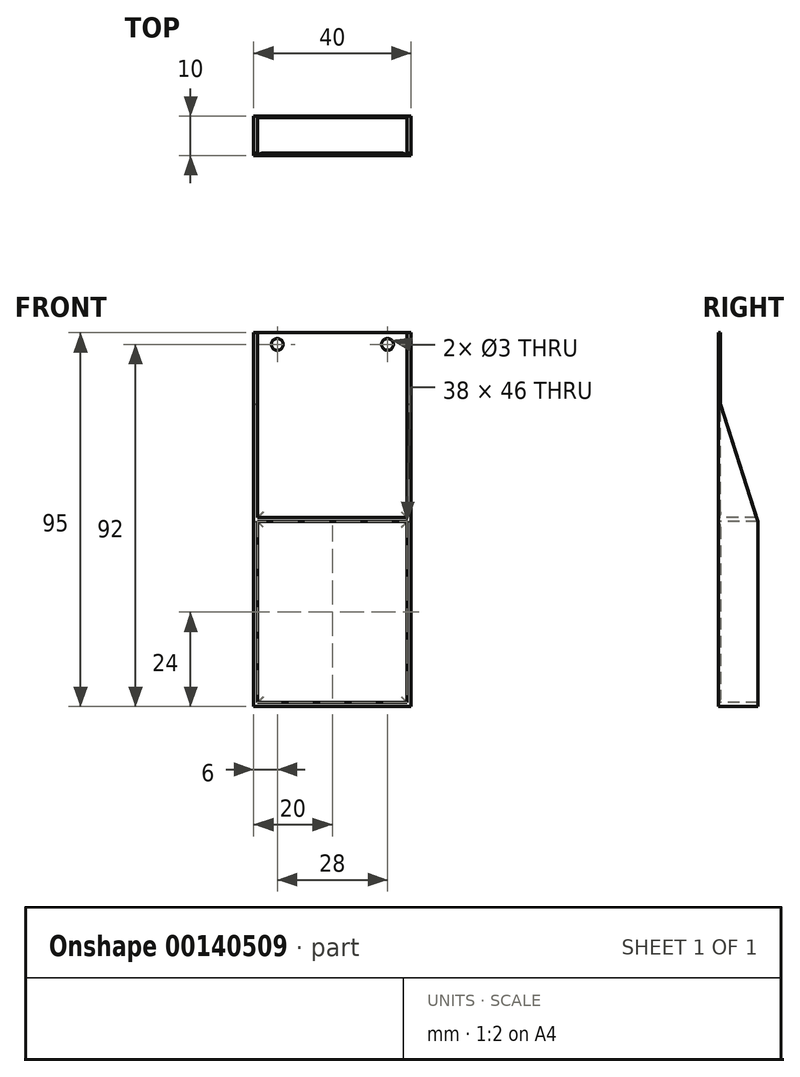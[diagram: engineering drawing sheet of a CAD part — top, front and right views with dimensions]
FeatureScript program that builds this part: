
annotation { "Feature Type Name" : "Feature", "Feature Type Description" : "" }
export const myFeature = defineFeature(function(context is Context, id is Id, definition is map)
    precondition{}
    {
        {
            var Q0;
            Q0=qCreatedBy(makeId("Front.planeOp"),FACE);
            var sketch = newSketch(context, id + "F0", { "sketchPlane" : qUnion([Q0])});
            skLineSegment(sketch, "E0.bottom", {"start": v(20, -47.5) * mm, "end": v(-20, -47.5) * mm});
            skLineSegment(sketch, "E0.top", {"start": v(20, 47.5) * mm, "end": v(-20, 47.5) * mm});
            skLineSegment(sketch, "E0.left", {"start": v(20, -47.5) * mm, "end": v(20, 47.5) * mm});
            skLineSegment(sketch, "E0.right", {"start": v(-20, -47.5) * mm, "end": v(-20, 47.5) * mm});
            skPoint(sketch, "E0.middle", {"position": v(0, 0) * mm});
            skLineSegment(sketch, "E1", {"start": v(-20, 47.5) * mm, "end": v(-19, 47.5) * mm});
            skLineSegment(sketch, "E2", {"start": v(-19, 47.5) * mm, "end": v(-19, 0.5) * mm});
            skLineSegment(sketch, "E3", {"start": v(20, -47.5) * mm, "end": v(19, -47.5) * mm});
            skLineSegment(sketch, "E4", {"start": v(19, -46.5) * mm, "end": v(19, -0.5) * mm});
            skLineSegment(sketch, "E5", {"start": v(-19, -46.5) * mm, "end": v(19, -46.5) * mm});
            skLineSegment(sketch, "E6", {"start": v(-19, 0.5) * mm, "end": v(19, 0.5) * mm});
            skLineSegment(sketch, "E7", {"start": v(19, -0.5) * mm, "end": v(-19, -0.5) * mm});
            skPoint(sketch, "E8.start.orphan", {"position": v(-19, 0) * mm});
            skLineSegment(sketch, "E9.trimOffspring", {"start": v(-19, -0.5) * mm, "end": v(-19, -46.5) * mm});
            skLineSegment(sketch, "E10.trimOffspring", {"start": v(19, 0.5) * mm, "end": v(19, 47.5) * mm});
            skPoint(sketch, "E11.start.orphan", {"position": v(-19, -47.5) * mm});
            skLineSegment(sketch, "E12", {"start": v(19, 47.5) * mm, "end": v(19, 44.5) * mm});
            skCircle(sketch, "E13", {"center": v(-14, 44.5) * mm, "radius": 1.5 * mm});
            skCircle(sketch, "E14", {"center": v(14, 44.5) * mm, "radius": 1.5 * mm});
            skSolve(sketch);
        }
        {
            var Q0;
            Q0=qCreatedBy(makeId("Right.planeOp"),FACE);
            var sketch = newSketch(context, id + "F1", { "sketchPlane" : qUnion([Q0])});
            skLineSegment(sketch, "E15", {"start": v(10, 31.26) * mm, "end": v(10, 64.46) * mm});
            skLineSegment(sketch, "E16", {"start": v(10, 64.46) * mm, "end": v(1, 64.46) * mm});
            skLineSegment(sketch, "E17", {"start": v(1, 28.09) * mm, "end": v(9.86, 0) * mm});
            skLineSegment(sketch, "E18", {"start": v(1, 28.09) * mm, "end": v(10, -0.46) * mm});
            skLineSegment(sketch, "E19", {"start": v(10, -0.46) * mm, "end": v(10, 31.26) * mm});
            skPoint(sketch, "E20", {"position": v(25.2, -48.64) * mm});
            skPoint(sketch, "E21.start.orphan", {"position": v(0, -48.64) * mm});
            skPoint(sketch, "E22.end.orphan", {"position": v(0, 31.26) * mm});
            skPoint(sketch, "E23.orphan", {"position": v(0, 64.46) * mm});
            skLineSegment(sketch, "E24", {"start": v(1, 28.09) * mm, "end": v(0.6, 29.36) * mm});
            skLineSegment(sketch, "E25", {"start": v(0.6, 64.46) * mm, "end": v(0.6, 29.36) * mm});
            skLineSegment(sketch, "E26", {"start": v(0.6, 64.46) * mm, "end": v(1, 64.46) * mm});
            skSolve(sketch);
        }
        {
            var Q0;
            Q0=makeQuery(id+"F0.imprint","IMPRINT",FACE,{"disambiguationData":[TD([[makeQuery(id+"F0.imprint","IMPRINT",EDGE,{"derivedFrom":sQuery(id+"F0.wireOp",EDGE,"E0.bottom")}),-1.0]])]});
            extrude(context, id + "F2", {"entities" : qUnion([Q0]), "oppositeDirection" : true, "depth" : 10 * mm});
        }
        {
            var Q0;
            {var subQ0=sQuery(id+"F0.wireOp",EDGE,"E2");Q0=makeQuery(id+"F0.imprint","IMPRINT",FACE,{"disambiguationData":[TD([[makeQuery(id+"F0.imprint","IMPRINT",EDGE,{"derivedFrom":subQ0}),1.0]])]});}
            var Q1;
            Q1=makeQuery(id+"F0.imprint","IMPRINT",FACE,{"disambiguationData":[TD([[makeQuery(id+"F0.imprint","IMPRINT",EDGE,{"derivedFrom":sQuery(id+"F0.wireOp",EDGE,"E4")}),1.0]])]});
            extrude(context, id + "F3", {"entities" : qUnion([Q0, Q1]), "oppositeDirection" : true, "depth" : 0.6 * mm});
        }
        {
            var Q0;
            Q0=makeQuery(id+"F3.opExtrude","CAP_EDGE",EDGE,{"disambiguationData":[OSD([sQuery(id+"F0.wireOp",EDGE,"E2")])],"isStart":false});
            var Q1;
            Q1=makeQuery(id+"F3.opExtrude","CAP_EDGE",EDGE,{"disambiguationData":[OSD([sQuery(id+"F0.wireOp",EDGE,"E6")])],"isStart":false});
            var Q2;
            Q2=makeQuery(id+"F3.opExtrude","CAP_EDGE",EDGE,{"disambiguationData":[OSD([sQuery(id+"F0.wireOp",EDGE,"E10.trimOffspring")])],"isStart":false});
            var Q3;
            Q3=makeQuery(id+"F3.opExtrude","CAP_EDGE",EDGE,{"disambiguationData":[OSD([sQuery(id+"F0.wireOp",EDGE,"E9.trimOffspring")])],"isStart":false});
            var Q4;
            Q4=makeQuery(id+"F3.opExtrude","CAP_EDGE",EDGE,{"disambiguationData":[OSD([sQuery(id+"F0.wireOp",EDGE,"E7")])],"isStart":false});
            var Q5;
            Q5=makeQuery(id+"F3.opExtrude","CAP_EDGE",EDGE,{"disambiguationData":[OSD([sQuery(id+"F0.wireOp",EDGE,"E4")])],"isStart":false});
            var Q6;
            Q6=makeQuery(id+"F3.opExtrude","CAP_EDGE",EDGE,{"disambiguationData":[OSD([sQuery(id+"F0.wireOp",EDGE,"E5")])],"isStart":false});
            fillet(context, id + "F4", {"entities" : qUnion([Q0, Q1, Q2, Q3, Q4, Q5, Q6]), "radius" : 2 * mm, "tangentPropagation" : true, "allowEdgeOverflow" : false});
        }
        {
            var Q0;
            Q0=makeQuery(id+"F1.imprint","IMPRINT",FACE,{"disambiguationData":[TD([[makeQuery(id+"F1.imprint","IMPRINT",EDGE,{"derivedFrom":sQuery(id+"F1.wireOp",EDGE,"E15")}),1.0]])]});
            extrude(context, id + "F5", {"entities" : qUnion([Q0]), "operationType" : NewBodyOperationType.REMOVE, "oppositeDirection" : true, "depth" : 25 * mm, "hasSecondDirection" : true, "secondDirectionOppositeDirection" : false, "secondDirectionDepth" : 25 * mm});
        }
    });
